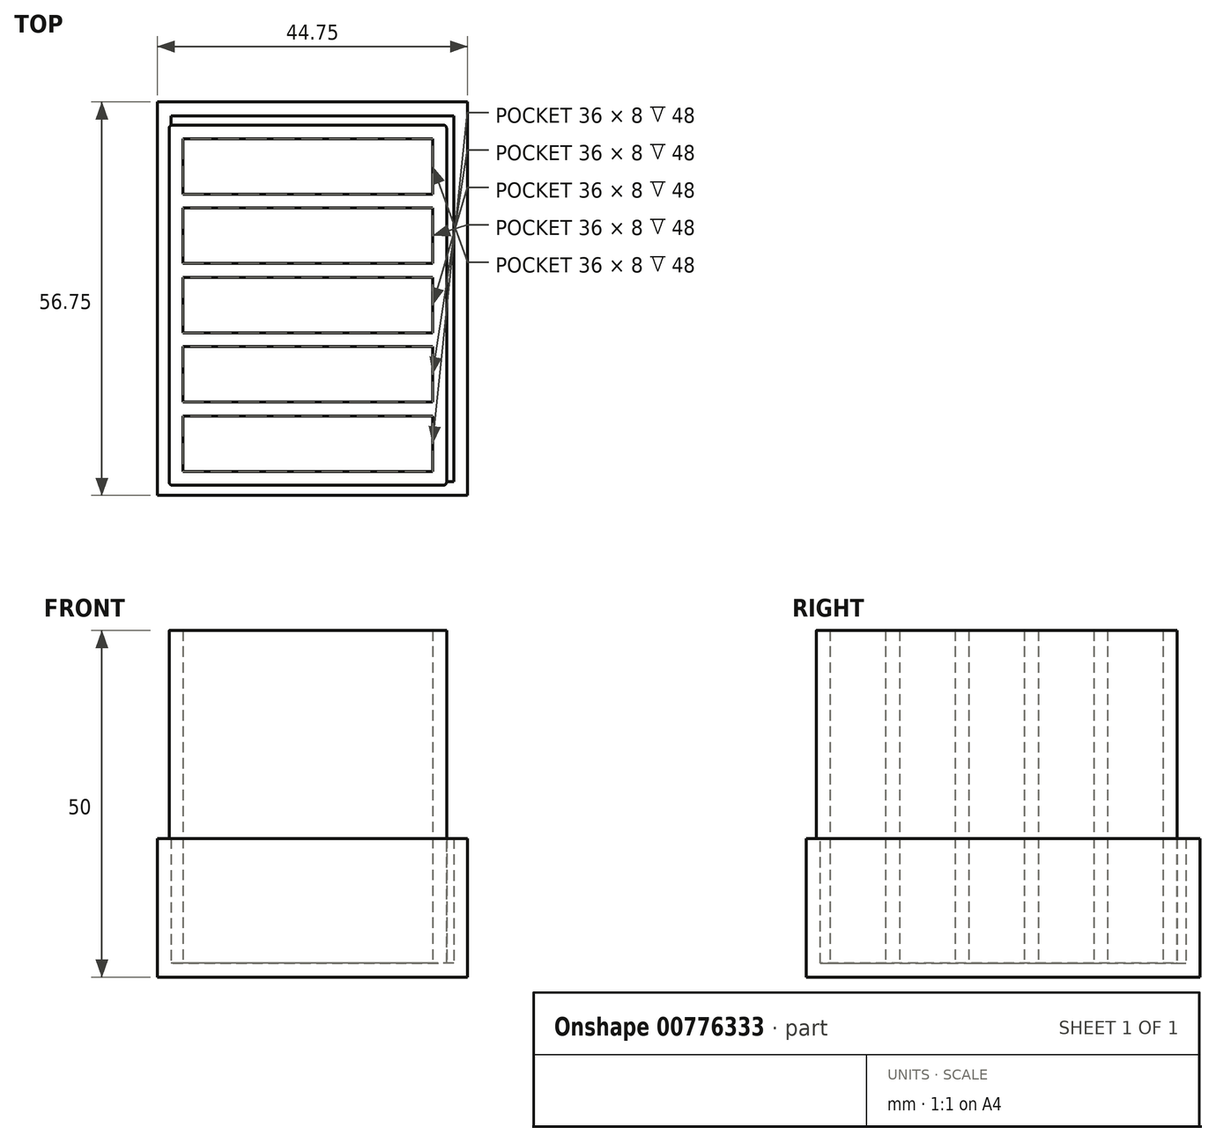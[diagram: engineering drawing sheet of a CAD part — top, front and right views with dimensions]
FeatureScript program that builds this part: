
annotation { "Feature Type Name" : "Feature", "Feature Type Description" : "" }
export const myFeature = defineFeature(function(context is Context, id is Id, definition is map)
    precondition{}
    {
        {
            var Q0;
            Q0=qCreatedBy(makeId("Top.planeOp"),FACE);
            var sketch = newSketch(context, id + "F0", { "sketchPlane" : qUnion([Q0])});
            skLineSegment(sketch, "E0.bottom", {"start": v(-62.27, 79.2) * mm, "end": v(-23.27, 79.2) * mm});
            skLineSegment(sketch, "E0.top", {"start": v(-62.27, 27.2) * mm, "end": v(-23.27, 27.2) * mm});
            skLineSegment(sketch, "E0.left", {"start": v(-62.77, 78.7) * mm, "end": v(-62.77, 27.7) * mm});
            skLineSegment(sketch, "E0.right", {"start": v(-22.77, 78.7) * mm, "end": v(-22.77, 27.7) * mm});
            skLineSegment(sketch, "E1.bottom", {"start": v(-60.77, 37.2) * mm, "end": v(-24.77, 37.2) * mm});
            skLineSegment(sketch, "E1.top", {"start": v(-60.77, 29.2) * mm, "end": v(-24.77, 29.2) * mm});
            skLineSegment(sketch, "E1.left", {"start": v(-60.77, 37.2) * mm, "end": v(-60.77, 29.2) * mm});
            skLineSegment(sketch, "E1.right", {"start": v(-24.77, 37.2) * mm, "end": v(-24.77, 29.2) * mm});
            skLineSegment(sketch, "E2.bottom", {"start": v(-60.77, 47.2) * mm, "end": v(-24.77, 47.2) * mm});
            skLineSegment(sketch, "E2.top", {"start": v(-60.77, 39.2) * mm, "end": v(-24.77, 39.2) * mm});
            skLineSegment(sketch, "E2.left", {"start": v(-60.77, 47.2) * mm, "end": v(-60.77, 39.2) * mm});
            skLineSegment(sketch, "E2.right", {"start": v(-24.77, 47.2) * mm, "end": v(-24.77, 39.2) * mm});
            skLineSegment(sketch, "E3.bottom", {"start": v(-60.77, 57.2) * mm, "end": v(-24.77, 57.2) * mm});
            skLineSegment(sketch, "E3.top", {"start": v(-60.77, 49.2) * mm, "end": v(-24.77, 49.2) * mm});
            skLineSegment(sketch, "E3.left", {"start": v(-60.77, 57.2) * mm, "end": v(-60.77, 49.2) * mm});
            skLineSegment(sketch, "E3.right", {"start": v(-24.77, 57.2) * mm, "end": v(-24.77, 49.2) * mm});
            skLineSegment(sketch, "E4.bottom", {"start": v(-60.77, 67.2) * mm, "end": v(-24.77, 67.2) * mm});
            skLineSegment(sketch, "E4.top", {"start": v(-60.77, 59.2) * mm, "end": v(-24.77, 59.2) * mm});
            skLineSegment(sketch, "E4.left", {"start": v(-60.77, 67.2) * mm, "end": v(-60.77, 59.2) * mm});
            skLineSegment(sketch, "E4.right", {"start": v(-24.77, 67.2) * mm, "end": v(-24.77, 59.2) * mm});
            skLineSegment(sketch, "E5.bottom", {"start": v(-60.77, 77.2) * mm, "end": v(-24.77, 77.2) * mm});
            skLineSegment(sketch, "E5.top", {"start": v(-60.77, 69.2) * mm, "end": v(-24.77, 69.2) * mm});
            skLineSegment(sketch, "E5.left", {"start": v(-60.77, 77.2) * mm, "end": v(-60.77, 69.2) * mm});
            skLineSegment(sketch, "E5.right", {"start": v(-24.77, 77.2) * mm, "end": v(-24.77, 69.2) * mm});
            skPoint(sketch, "E6.visualSharp", {"position": v(-62.77, 79.2) * mm});
            skArc(sketch, "E6.filletArc", {"start": v(-62.27, 79.2) * mm, "mid": v(-62.63, 79.05) * mm, "end": v(-62.77, 78.7) * mm});
            skPoint(sketch, "E7.visualSharp", {"position": v(-22.77, 79.2) * mm});
            skArc(sketch, "E7.filletArc", {"start": v(-22.77, 78.7) * mm, "mid": v(-22.92, 79.05) * mm, "end": v(-23.27, 79.2) * mm});
            skPoint(sketch, "E8.visualSharp", {"position": v(-22.77, 27.2) * mm});
            skArc(sketch, "E8.filletArc", {"start": v(-23.27, 27.2) * mm, "mid": v(-22.92, 27.34) * mm, "end": v(-22.77, 27.7) * mm});
            skPoint(sketch, "E9.visualSharp", {"position": v(-62.77, 27.2) * mm});
            skArc(sketch, "E9.filletArc", {"start": v(-62.77, 27.7) * mm, "mid": v(-62.63, 27.34) * mm, "end": v(-62.27, 27.2) * mm});
            skSolve(sketch);
        }
        {
            var Q0;
            Q0=makeQuery(id+"F0.imprint","IMPRINT",FACE,{"disambiguationData":[TD([[makeQuery(id+"F0.imprint","IMPRINT",EDGE,{"derivedFrom":sQuery(id+"F0.wireOp",EDGE,"E1.bottom")}),-1.0]])]});
            var Q1;
            Q1=makeQuery(id+"F0.imprint","IMPRINT",FACE,{"disambiguationData":[TD([[makeQuery(id+"F0.imprint","IMPRINT",EDGE,{"derivedFrom":sQuery(id+"F0.wireOp",EDGE,"E0.bottom")}),-1.0]])]});
            var Q2;
            Q2=makeQuery(id+"F0.imprint","IMPRINT",FACE,{"disambiguationData":[TD([[makeQuery(id+"F0.imprint","IMPRINT",EDGE,{"derivedFrom":sQuery(id+"F0.wireOp",EDGE,"E2.bottom")}),-1.0]])]});
            var Q3;
            Q3=makeQuery(id+"F0.imprint","IMPRINT",FACE,{"disambiguationData":[TD([[makeQuery(id+"F0.imprint","IMPRINT",EDGE,{"derivedFrom":sQuery(id+"F0.wireOp",EDGE,"E3.bottom")}),-1.0]])]});
            var Q4;
            Q4=makeQuery(id+"F0.imprint","IMPRINT",FACE,{"disambiguationData":[TD([[makeQuery(id+"F0.imprint","IMPRINT",EDGE,{"derivedFrom":sQuery(id+"F0.wireOp",EDGE,"E4.bottom")}),-1.0]])]});
            var Q5;
            Q5=makeQuery(id+"F0.imprint","IMPRINT",FACE,{"disambiguationData":[TD([[makeQuery(id+"F0.imprint","IMPRINT",EDGE,{"derivedFrom":sQuery(id+"F0.wireOp",EDGE,"E5.bottom")}),-1.0]])]});
            extrude(context, id + "F1", {"entities" : qUnion([Q0, Q1, Q2, Q3, Q4, Q5]), "depth" : 2 * mm, "offsetDistance" : 25 * mm});
        }
        {
            var Q0;
            Q0=makeQuery(id+"F0.imprint","IMPRINT",FACE,{"disambiguationData":[TD([[makeQuery(id+"F0.imprint","IMPRINT",EDGE,{"derivedFrom":sQuery(id+"F0.wireOp",EDGE,"E0.bottom")}),-1.0]])]});
            extrude(context, id + "F2", {"entities" : qUnion([Q0]), "operationType" : NewBodyOperationType.ADD, "depth" : 50 * mm, "offsetDistance" : 25 * mm});
        }
        {
            var Q0;
            Q0=qCreatedBy(makeId("Top.planeOp"),FACE);
            var sketch = newSketch(context, id + "F3", { "sketchPlane" : qUnion([Q0])});
            skLineSegment(sketch, "E10.bottom", {"start": v(-64.48, 82.5) * mm, "end": v(-19.73, 82.5) * mm});
            skLineSegment(sketch, "E10.top", {"start": v(-64.48, 25.75) * mm, "end": v(-19.73, 25.75) * mm});
            skLineSegment(sketch, "E10.left", {"start": v(-64.48, 82.5) * mm, "end": v(-64.48, 25.75) * mm});
            skLineSegment(sketch, "E10.right", {"start": v(-19.73, 82.5) * mm, "end": v(-19.73, 25.75) * mm});
            skLineSegment(sketch, "E11.bottom", {"start": v(-62.48, 80.5) * mm, "end": v(-21.73, 80.5) * mm});
            skLineSegment(sketch, "E11.top", {"start": v(-62.48, 27.75) * mm, "end": v(-21.73, 27.75) * mm});
            skLineSegment(sketch, "E11.left", {"start": v(-62.48, 80.5) * mm, "end": v(-62.48, 27.75) * mm});
            skLineSegment(sketch, "E11.right", {"start": v(-21.73, 80.5) * mm, "end": v(-21.73, 27.75) * mm});
            skSolve(sketch);
        }
        {
            var Q0;
            Q0=makeQuery(id+"F3.imprint","IMPRINT",FACE,{"disambiguationData":[TD([[makeQuery(id+"F3.imprint","IMPRINT",EDGE,{"derivedFrom":sQuery(id+"F3.wireOp",EDGE,"E10.bottom")}),-1.0]])]});
            var Q1;
            Q1=makeQuery(id+"F3.imprint","IMPRINT",FACE,{"disambiguationData":[TD([[makeQuery(id+"F3.imprint","IMPRINT",EDGE,{"derivedFrom":sQuery(id+"F3.wireOp",EDGE,"E11.bottom")}),-1.0]])]});
            extrude(context, id + "F4", {"entities" : qUnion([Q0, Q1]), "depth" : 2 * mm, "offsetDistance" : 25 * mm});
        }
        {
            var Q0;
            Q0=makeQuery(id+"F3.imprint","IMPRINT",FACE,{"disambiguationData":[TD([[makeQuery(id+"F3.imprint","IMPRINT",EDGE,{"derivedFrom":sQuery(id+"F3.wireOp",EDGE,"E10.bottom")}),-1.0]])]});
            extrude(context, id + "F5", {"entities" : qUnion([Q0]), "operationType" : NewBodyOperationType.ADD, "depth" : 20 * mm, "offsetDistance" : 25 * mm});
        }
    });
